# Revit family: ALRR
name_source: partatom
category: Lighting Fixtures
units: mm (PartAtom-declared; Revit-internal decimal feet)

## family parameters
Always vertical = Yes
Cut with Voids When Loaded = No
Host = Ceiling
Light Source = Yes
Maintain Annotation Orientation = No
OmniClass Number = 23.80.70.11.14.17
OmniClass Title = Direct/Indirect
Part Type = Normal
Room Calculation Point = No
Round Connector Dimension = Use Diameter
Shared = No

## types (14) — shared parameters
Assembly Code = D5020200
Color Filter = 16777215
Default Elevation = 0' - 0"
Description = LED- Premium-Grade Suspended Linear Luminaire
Dimming Lamp Color Temperature Shift = <None>
Emit from Line Length = 4' - 0 3/32"
Housing Finish = Metal - Viscor - White
Lamp = LED
Length = 4' - 0 3/32"
Lens Finish Bottom = Acrylic - Viscor - Frosted
Lens Finish Top = Acrylic - Viscor - Clear
Manufacturer = VISIONEERING by VISCOR
Model = ALRR
Tilt Angle = 180.00°
URL = https://viscor.com
Voltage = 120 V
Width = 0' - 7 5/8"

## per-type parameters (varying)
| type | Apparent Load | Lamp Wattage | Photometric Web File |
| ALRR48-LED840K05LFUNV-LD72 | 15 VA | 15 VA | ALRR48-LED840K05LFUNV-LD72.ies |
| ALRR48-LED840K05LFUNV-LD91 | 15 VA | 15 VA | ALRR48-LED840K05LFUNV-LD91.ies |
| ALRR48-LED840K7.5LFUNV-LD72 | 22 VA | 22 VA | ALRR48-LED840K7.5LFUNV-LD72.ies |
| ALRR48-LED840K7.5LFUNV-LD91 | 22 VA | 22 VA | ALRR48-LED840K7.5LFUNV-LD91.ies |
| ALRR48-LED840K10LFUNV-LD72 | 29 VA | 29 VA | ALRR48-LED840K10LFUNV-LD72.ies |
| ALRR48-LED840K10LFUNV-LD91 | 29 VA | 29 VA | ALRR48-LED840K10LFUNV-LD91.ies |
| ALRR48-LED840K12.5LFUNV-LD72 | 37 VA | 37 VA | ALRR48-LED840K12.5LFUNV-LD72.ies |
| ALRR48-LED840K12.5LFUNV-LD91 | 37 VA | 37 VA | ALRR48-LED840K12.5LFUNV-LD91.ies |
| ALRR48-LED840K15LFUNV-LD72 | 44 VA | 44 VA | ALRR48-LED840K15LFUNV-LD72.ies |
| ALRR48-LED840K15LFUNV-LD91 | 44 VA | 44 VA | ALRR48-LED840K15LFUNV-LD91.ies |
| ALRR48-LED840K17.5LFUNV-LD72 | 52 VA | 52 VA | ALRR48-LED840K17.5LFUNV-LD72.ies |
| ALRR48-LED840K17.5LFUNV-LD91 | 52 VA | 52 VA | ALRR48-LED840K17.5LFUNV-LD91.ies |
| ALRR48-LED840K20LFUNV-LD72 | 59 VA | 59 VA | ALRR48-LED840K20LFUNV-LD72.ies |
| ALRR48-LED840K20LFUNV-LD91 | 59 VA | 59 VA | ALRR48-LED840K20LFUNV-LD91.ies |

## geometry (parser evidence)
native form markers: Sweep x2
no freeform markers — native parametric forms only
